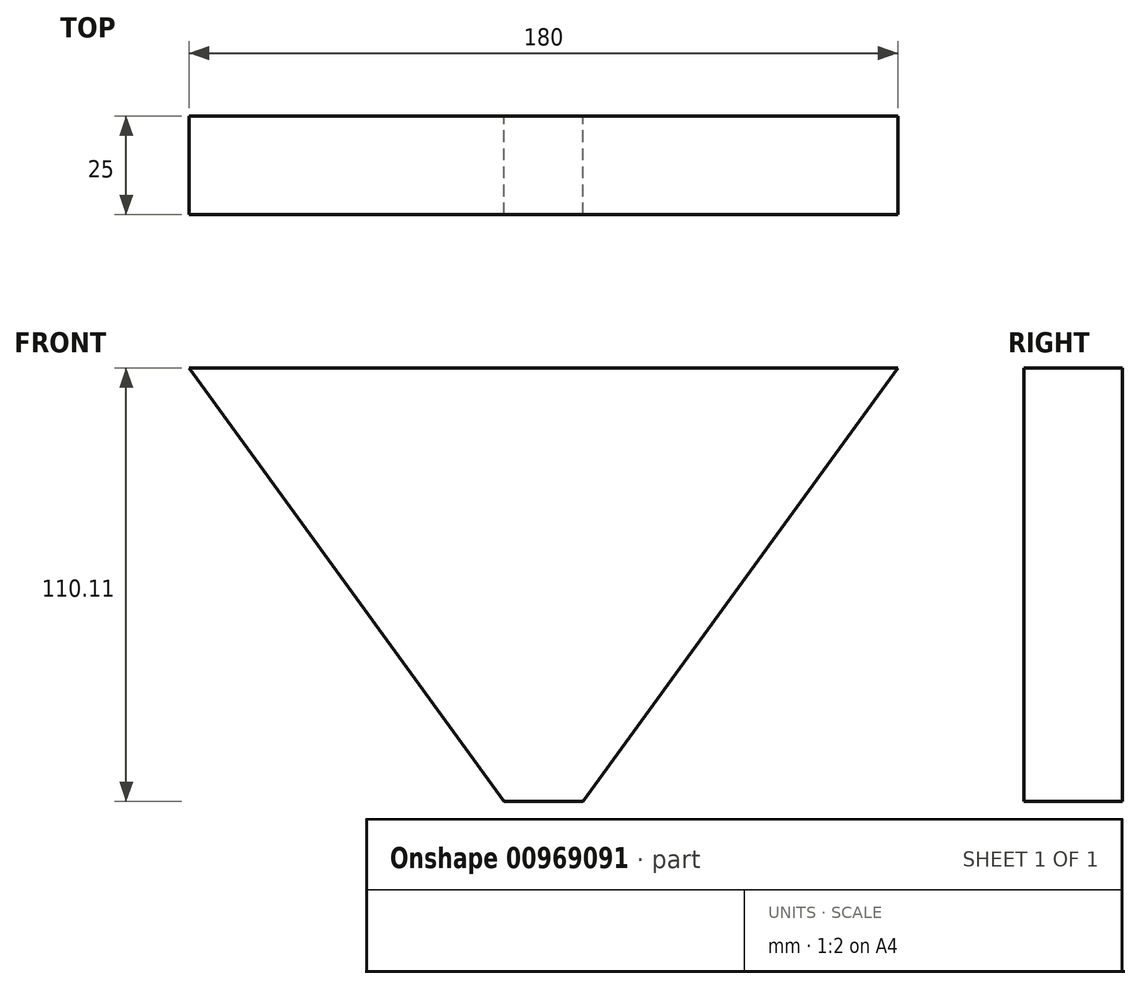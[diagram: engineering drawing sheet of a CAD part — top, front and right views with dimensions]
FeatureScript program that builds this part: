
annotation { "Feature Type Name" : "Feature", "Feature Type Description" : "" }
export const myFeature = defineFeature(function(context is Context, id is Id, definition is map)
    precondition{}
    {
        {
            var Q0;
            Q0=qCreatedBy(makeId("Front.planeOp"),FACE);
            var sketch = newSketch(context, id + "F0", { "sketchPlane" : qUnion([Q0])});
            skLineSegment(sketch, "E0", {"start": v(0, 0) * mm, "end": v(-20, 0) * mm});
            skLineSegment(sketch, "E1", {"start": v(-20, 0) * mm, "end": v(-100, 110.11) * mm});
            skLineSegment(sketch, "E2", {"start": v(-100, 110.11) * mm, "end": v(80, 110.11) * mm});
            skLineSegment(sketch, "E3", {"start": v(80, 110.11) * mm, "end": v(0, 0) * mm});
            skSolve(sketch);
        }
        {
            var Q0;
            Q0 = qSketchRegion(id + "F0", true);
            extrude(context, id + "F1", {"entities" : qUnion([Q0]), "depth" : 25 * mm, "offsetDistance" : 25 * mm});
        }
    });
